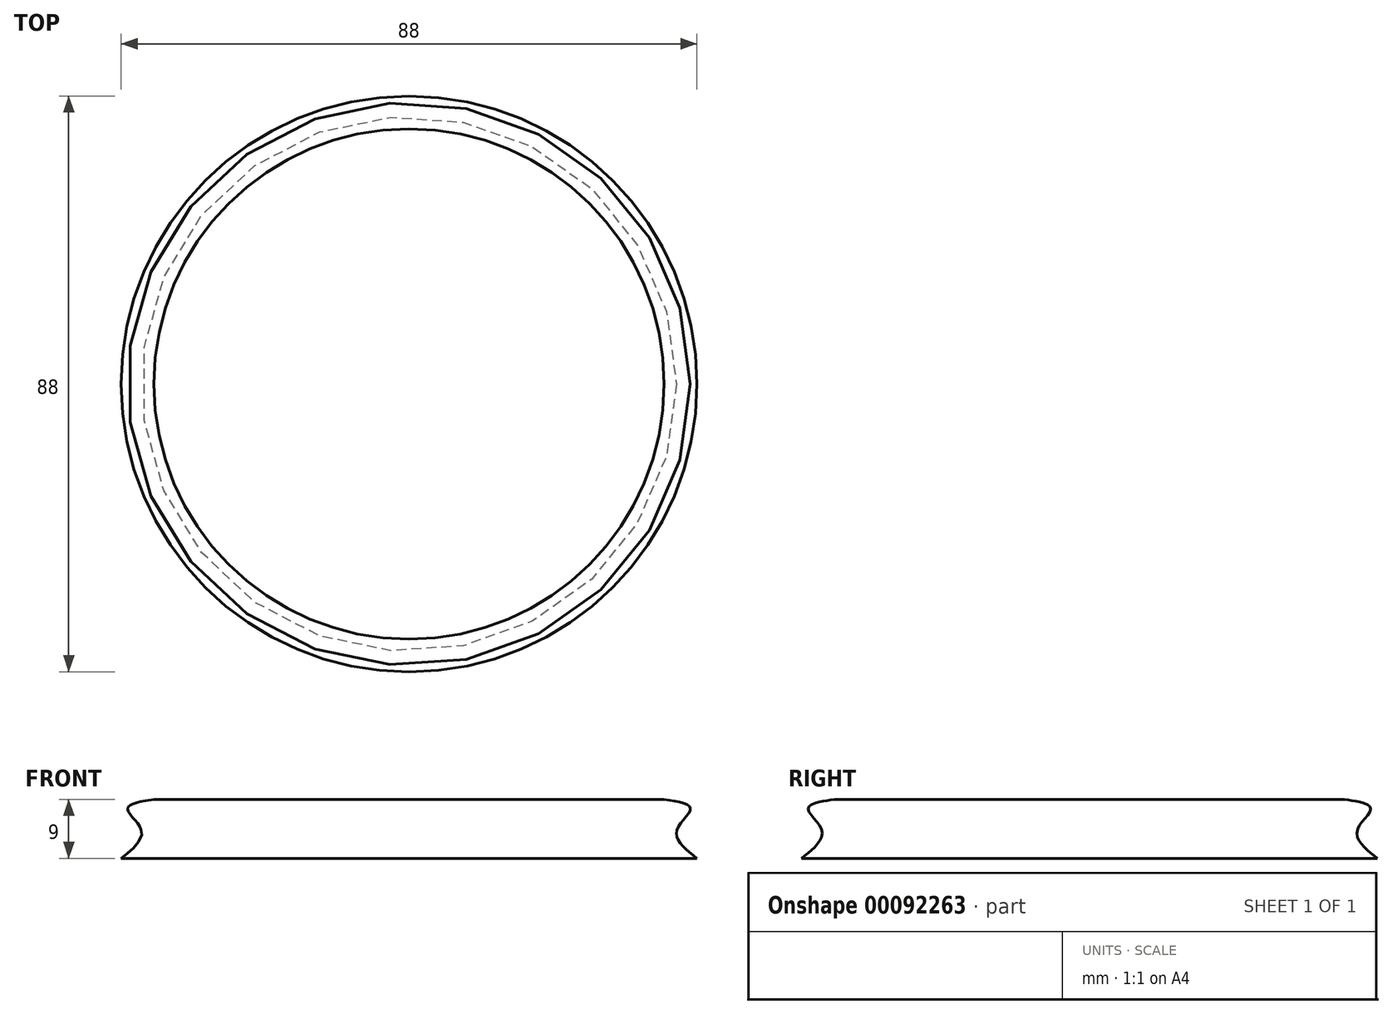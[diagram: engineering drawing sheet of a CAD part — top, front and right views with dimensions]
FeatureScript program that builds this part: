
annotation { "Feature Type Name" : "Feature", "Feature Type Description" : "" }
export const myFeature = defineFeature(function(context is Context, id is Id, definition is map)
    precondition{}
    {
        {
            var Q0;
            Q0=qCreatedBy(makeId("Top.planeOp"),FACE);
            var sketch = newSketch(context, id + "F0", { "sketchPlane" : qUnion([Q0])});
            skCircle(sketch, "E0", {"center": v(0, 0) * mm, "radius": 44 * mm});
            skSolve(sketch);
        }
        {
            var Q0;
            Q0=qCreatedBy(makeId("Top.planeOp"),FACE);
            cPlane(context, id + "F1", {"entities" : qUnion([Q0]), "cplaneType" : CPlaneType.OFFSET, "offset" : 4.5 * mm, "width" : 150 * mm, "height" : 150 * mm});
        }
        {
            var Q0;
            Q0=qCreatedBy(id+"F1.planeOp",FACE);
            var sketch = newSketch(context, id + "F2", { "sketchPlane" : qUnion([Q0])});
            skCircle(sketch, "E1", {"center": v(0, 0) * mm, "radius": 41 * mm});
            skSolve(sketch);
        }
        {
            var Q0;
            Q0=qCreatedBy(id+"F1.planeOp",FACE);
            cPlane(context, id + "F3", {"entities" : qUnion([Q0]), "cplaneType" : CPlaneType.OFFSET, "offset" : 3 * mm, "width" : 150 * mm, "height" : 150 * mm});
        }
        {
            var Q0;
            Q0=qCreatedBy(id+"F3.planeOp",FACE);
            var sketch = newSketch(context, id + "F4", { "sketchPlane" : qUnion([Q0])});
            skCircle(sketch, "E2", {"center": v(0, 0) * mm, "radius": 43 * mm});
            skSolve(sketch);
        }
        {
            var Q0;
            Q0=qCreatedBy(id+"F3.planeOp",FACE);
            cPlane(context, id + "F5", {"entities" : qUnion([Q0]), "cplaneType" : CPlaneType.OFFSET, "offset" : 1.5 * mm, "width" : 150 * mm, "height" : 150 * mm});
        }
        {
            var Q0;
            Q0=qCreatedBy(id+"F5.planeOp",FACE);
            var sketch = newSketch(context, id + "F6", { "sketchPlane" : qUnion([Q0])});
            skCircle(sketch, "E3", {"center": v(0, 0) * mm, "radius": 39 * mm});
            skSolve(sketch);
        }
        {
            var Q0;
            Q0=qCreatedBy(makeId("Right.planeOp"),FACE);
            var sketch = newSketch(context, id + "F7", { "sketchPlane" : qUnion([Q0])});
            skArc(sketch, "E4", {"start": v(-40.97, 4.47) * mm, "mid": v(-43.1, 2.65) * mm, "end": v(-44, 0) * mm, "construction": true});
            skSolve(sketch);
        }
        {
            var Q0;
            Q0=sQuery(id+"F6.wireOp",EDGE,"E3");
            var Q1;
            Q1=sQuery(id+"F4.wireOp",EDGE,"E2");
            var Q2;
            Q2=sQuery(id+"F2.wireOp",EDGE,"E1");
            var Q3;
            Q3=sQuery(id+"F0.wireOp",EDGE,"E0");
            var Q4;
            Q4 = qConstructionFilter(qBodyType(qCreatedBy(id + "F7" ,EDGE), BodyType.WIRE), ConstructionObject.NO);
            loft(context, id + "F8", {"bodyType" : ToolBodyType.SURFACE, "addGuides" : true, "wireProfilesArray" : [{ "wireProfileEntities" : qUnion([Q0]) }, { "wireProfileEntities" : qUnion([Q1]) }, { "wireProfileEntities" : qUnion([Q2]) }, { "wireProfileEntities" : qUnion([Q3]) }], "guidesArray" : [{ "guideEntities" : qUnion([Q4]), "guideDerivativeType" : LoftGuideDerivativeType.DEFAULT, "guideDerivativeMagnitude" : 1 }]});
        }
    });
